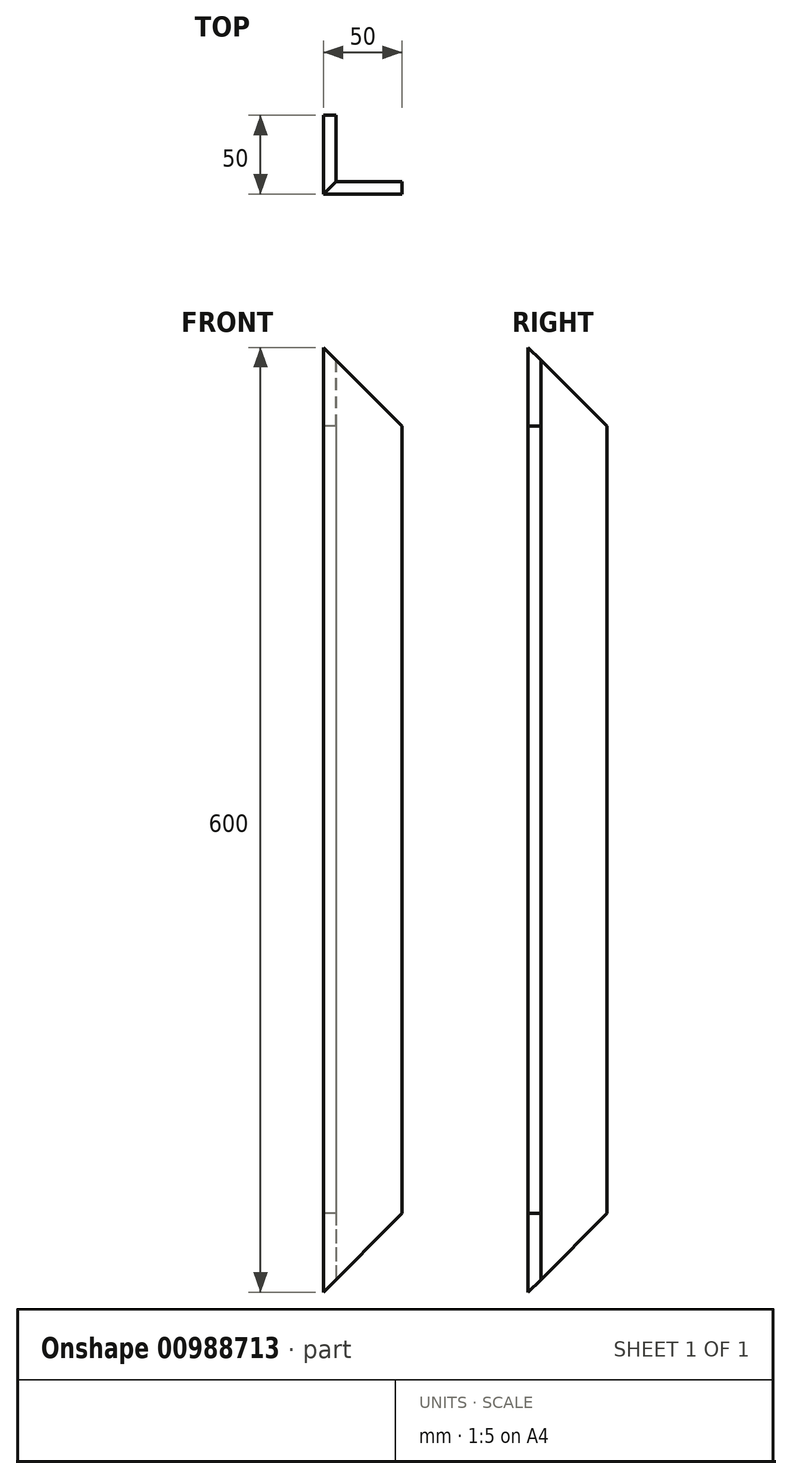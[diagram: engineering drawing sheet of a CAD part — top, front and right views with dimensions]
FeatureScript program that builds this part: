
annotation { "Feature Type Name" : "Feature", "Feature Type Description" : "" }
export const myFeature = defineFeature(function(context is Context, id is Id, definition is map)
    precondition{}
    {
        {
            var Q0;
            Q0=qCreatedBy(makeId("Top.planeOp"),FACE);
            var sketch = newSketch(context, id + "F0", { "sketchPlane" : qUnion([Q0])});
            skLineSegment(sketch, "E0", {"start": v(0, 0) * mm, "end": v(0, 50) * mm});
            skLineSegment(sketch, "E1", {"start": v(0, 50) * mm, "end": v(8, 50) * mm});
            skLineSegment(sketch, "E2", {"start": v(8, 50) * mm, "end": v(8, 8) * mm});
            skLineSegment(sketch, "E3", {"start": v(8, 8) * mm, "end": v(50, 8) * mm});
            skLineSegment(sketch, "E4", {"start": v(50, 8) * mm, "end": v(50, 0) * mm});
            skLineSegment(sketch, "E5", {"start": v(50, 0) * mm, "end": v(0, 0) * mm});
            skSolve(sketch);
        }
        {
            var Q0;
            Q0=qSketchRegion(id+"F0",true);
            extrude(context, id + "F1", {"entities" : qUnion([Q0]), "depth" : 600 * mm, "offsetDistance" : 25 * mm});
        }
        {
            var Q0;
            Q0=makeQuery(id+"F1.opExtrude","SWEPT_FACE",FACE,{"disambiguationData":[OSD([sQuery(id+"F0.wireOp",EDGE,"E5")])]});
            var sketch = newSketch(context, id + "F2", { "sketchPlane" : qUnion([Q0])});
            skLineSegment(sketch, "E6", {"start": v(0, 600) * mm, "end": v(50, 550) * mm});
            skLineSegment(sketch, "E7", {"start": v(50, 550) * mm, "end": v(50, 600) * mm});
            skLineSegment(sketch, "E8", {"start": v(50, 600) * mm, "end": v(0, 600) * mm});
            skSolve(sketch);
        }
        {
            var Q0;
            Q0=makeQuery(id+"F2.imprint","IMPRINT",FACE,{"disambiguationData":[TD([[makeQuery(id+"F2.imprint","IMPRINT",EDGE,{"derivedFrom":sQuery(id+"F2.wireOp",EDGE,"E6")}),1.0]])]});
            var Q1;
            Q1=makeQuery(id+"F1.opExtrude","SWEPT_FACE",FACE,{"disambiguationData":[OSD([sQuery(id+"F0.wireOp",EDGE,"E3")])]});
            extrude(context, id + "F3", {"entities" : qUnion([Q0]), "operationType" : NewBodyOperationType.REMOVE, "endBound" : BoundingType.UP_TO_SURFACE, "oppositeDirection" : true, "depth" : 25 * mm, "endBoundEntityFace" : qUnion([Q1]), "offsetDistance" : 25 * mm});
        }
        {
            var Q0;
            Q0=makeQuery(id+"F1.opExtrude","SWEPT_FACE",FACE,{"disambiguationData":[OSD([sQuery(id+"F0.wireOp",EDGE,"E0")])]});
            var sketch = newSketch(context, id + "F4", { "sketchPlane" : qUnion([Q0])});
            skLineSegment(sketch, "E9", {"start": v(0, 600) * mm, "end": v(0, 550) * mm});
            skLineSegment(sketch, "E10", {"start": v(0, 550) * mm, "end": v(-50, 550) * mm});
            skLineSegment(sketch, "E11", {"start": v(-50, 550) * mm, "end": v(0, 600) * mm});
            skSolve(sketch);
        }
        {
            var Q0;
            {var subQ0=sQuery(id+"F4.wireOp",EDGE,"E11");Q0=makeQuery(id+"F4.imprint","IMPRINT",FACE,{"disambiguationData":[TD([[makeQuery(id+"F4.imprint","IMPRINT",EDGE,{"derivedFrom":subQ0}),1.0]])]});}
            var Q1;
            Q1=makeQuery(id+"F1.opExtrude","SWEPT_FACE",FACE,{"disambiguationData":[OSD([sQuery(id+"F0.wireOp",EDGE,"E2")])]});
            extrude(context, id + "F5", {"entities" : qUnion([Q0]), "operationType" : NewBodyOperationType.REMOVE, "endBound" : BoundingType.UP_TO_SURFACE, "oppositeDirection" : true, "depth" : 25 * mm, "endBoundEntityFace" : qUnion([Q1]), "offsetDistance" : 25 * mm});
        }
        {
            var Q0;
            Q0=makeQuery(id+"F1.opExtrude","SWEPT_FACE",FACE,{"disambiguationData":[OSD([sQuery(id+"F0.wireOp",EDGE,"E5")])]});
            var sketch = newSketch(context, id + "F6", { "sketchPlane" : qUnion([Q0])});
            skLineSegment(sketch, "E12", {"start": v(0, 0) * mm, "end": v(50, 0) * mm});
            skLineSegment(sketch, "E13", {"start": v(50, 0) * mm, "end": v(50, 50) * mm});
            skLineSegment(sketch, "E14", {"start": v(50, 50) * mm, "end": v(0, 0) * mm});
            skSolve(sketch);
        }
        {
            var Q0;
            Q0=makeQuery(id+"F6.imprint","IMPRINT",FACE,{"disambiguationData":[TD([[makeQuery(id+"F6.imprint","IMPRINT",EDGE,{"derivedFrom":sQuery(id+"F6.wireOp",EDGE,"E12")}),-1.0]])]});
            var Q1;
            Q1=makeQuery(id+"F1.opExtrude","SWEPT_FACE",FACE,{"disambiguationData":[OSD([sQuery(id+"F0.wireOp",EDGE,"E3")])]});
            extrude(context, id + "F7", {"entities" : qUnion([Q0]), "operationType" : NewBodyOperationType.REMOVE, "endBound" : BoundingType.UP_TO_SURFACE, "oppositeDirection" : true, "depth" : 25 * mm, "endBoundEntityFace" : qUnion([Q1]), "offsetDistance" : 25 * mm});
        }
        {
            var Q0;
            Q0=makeQuery(id+"F1.opExtrude","SWEPT_FACE",FACE,{"disambiguationData":[OSD([sQuery(id+"F0.wireOp",EDGE,"E0")])]});
            var sketch = newSketch(context, id + "F8", { "sketchPlane" : qUnion([Q0])});
            skLineSegment(sketch, "E15", {"start": v(0, 0) * mm, "end": v(-50, 0) * mm});
            skLineSegment(sketch, "E16", {"start": v(-50, 0) * mm, "end": v(-50, 50) * mm});
            skLineSegment(sketch, "E17", {"start": v(-50, 50) * mm, "end": v(0, 0) * mm});
            skSolve(sketch);
        }
        {
            var Q0;
            {var subQ3=sQuery(id+"F8.wireOp",EDGE,"E16");Q0=makeQuery(id+"F8.imprint","IMPRINT",FACE,{"disambiguationData":[TD([[makeQuery(id+"F8.imprint","IMPRINT",EDGE,{"derivedFrom":subQ3}),1.0]])]});}
            var Q1;
            Q1=makeQuery(id+"F1.opExtrude","SWEPT_FACE",FACE,{"disambiguationData":[OSD([sQuery(id+"F0.wireOp",EDGE,"E2")])]});
            extrude(context, id + "F9", {"entities" : qUnion([Q0]), "operationType" : NewBodyOperationType.REMOVE, "endBound" : BoundingType.UP_TO_SURFACE, "oppositeDirection" : true, "depth" : 25 * mm, "endBoundEntityFace" : qUnion([Q1]), "offsetDistance" : 25 * mm});
        }
    });
